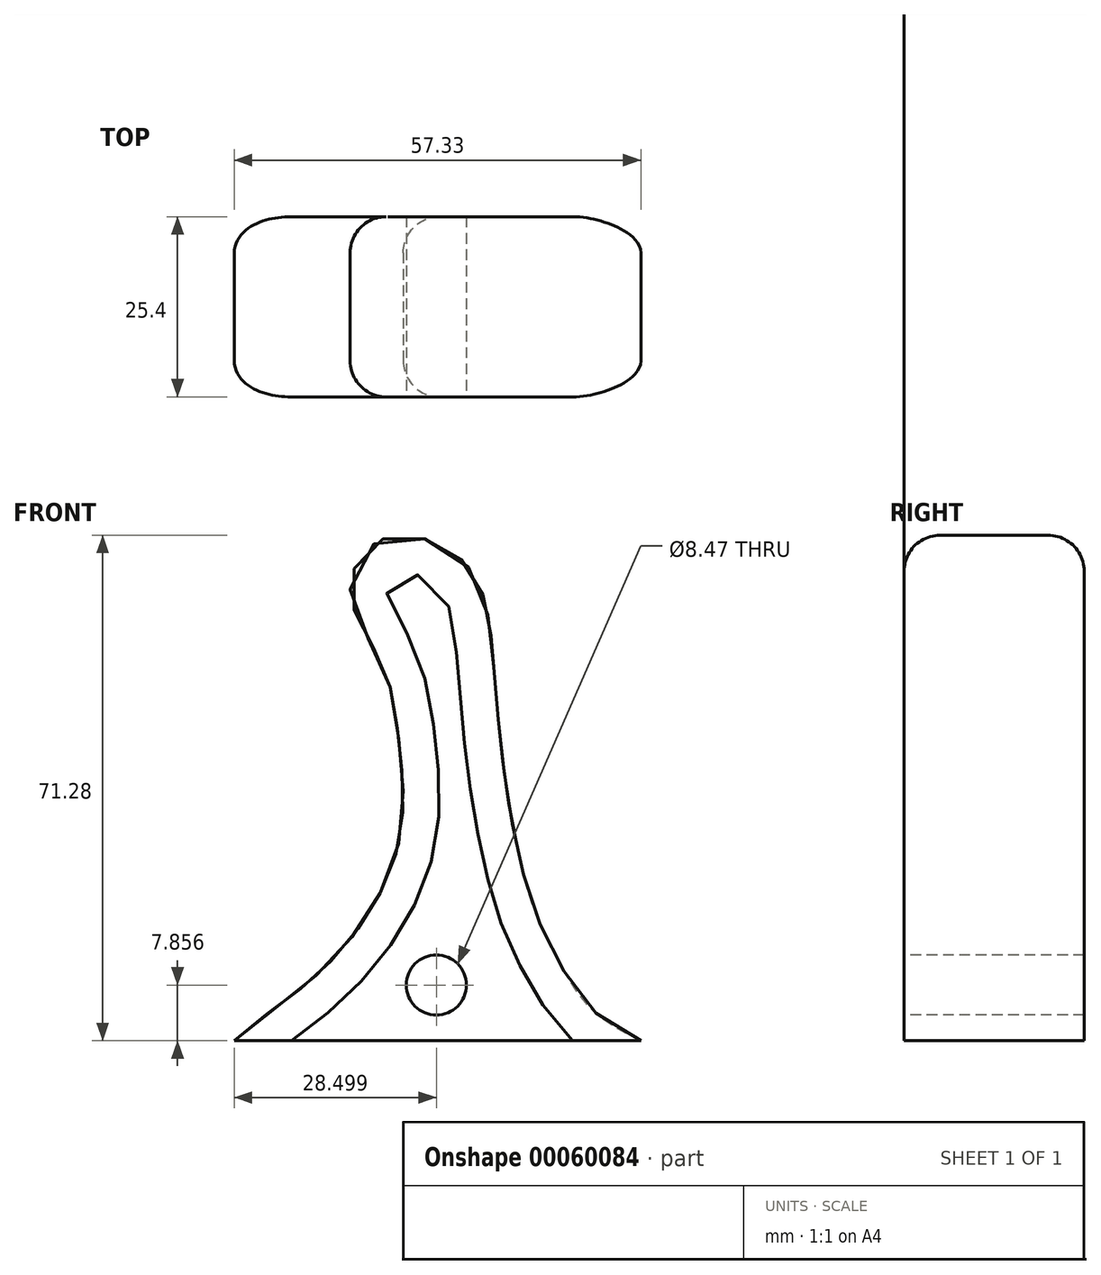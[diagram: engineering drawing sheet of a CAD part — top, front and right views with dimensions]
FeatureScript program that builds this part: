
annotation { "Feature Type Name" : "Feature", "Feature Type Description" : "" }
export const myFeature = defineFeature(function(context is Context, id is Id, definition is map)
    precondition{}
    {
        {
            var Q0;
            Q0=qCreatedBy(makeId("Front.planeOp"),FACE);
            var sketch = newSketch(context, id + "F0", { "sketchPlane" : qUnion([Q0])});
            skFitSpline(sketch, "E0", {"points": [v(-35.6, 0) * mm, v(-27.25, 6.54) * mm, v(-19.41, 14.14) * mm, v(-13.96, 23.16) * mm, v(-11.82, 32.41) * mm, v(-12.53, 43.57) * mm, v(-14.9, 53.3) * mm, v(-19.27, 63.82) * mm, v(-14.4, 70.87) * mm, v(-6.42, 69.77) * mm, v(-2.15, 66.2) * mm, v(0, 60.75) * mm, v(1.27, 49.42) * mm, v(2.84, 35.12) * mm, v(4.78, 25.1) * mm, v(7.04, 17.63) * mm, v(11.13, 9.44) * mm, v(15.79, 3.52) * mm, v(21.72, 0) * mm], "startDerivative": vector(113.36, 115.6) * mm, "endDerivative": vector(129.53, -62.93) * mm});
            skLineSegment(sketch, "E1", {"start": v(-35.6, 0) * mm, "end": v(21.72, 0) * mm});
            skSolve(sketch);
        }
        {
            var Q0;
            Q0=makeQuery(id+"F0.imprint","IMPRINT",FACE,{"disambiguationData":[TD([[makeQuery(id+"F0.imprint","IMPRINT",EDGE,{"derivedFrom":sQuery(id+"F0.wireOp",EDGE,"E0")}),-1.0]])]});
            extrude(context, id + "F1", {"entities" : qUnion([Q0]), "depth" : 25.4 * mm});
        }
        {
            var Q0;
            Q0=makeQuery(id+"F1.opExtrude","CAP_EDGE",EDGE,{"disambiguationData":[OSD([sQuery(id+"F0.wireOp",EDGE,"E0")])],"isStart":false});
            var Q1;
            Q1=makeQuery(id+"F1.opExtrude","CAP_EDGE",EDGE,{"disambiguationData":[OSD([sQuery(id+"F0.wireOp",EDGE,"E0")])],"isStart":true});
            fillet(context, id + "F2", {"entities" : qUnion([Q0, Q1]), "radius" : 5.08 * mm, "tangentPropagation" : true, "allowEdgeOverflow" : false});
        }
        {
            var Q0;
            Q0=makeQuery(id+"F1.opExtrude","CAP_FACE",FACE,{"disambiguationData":[OSD([sQuery(id+"F0.wireOp",EDGE,"E0"),sQuery(id+"F0.wireOp",EDGE,"E1")])],"isStart":false});
            var sketch = newSketch(context, id + "F3", { "sketchPlane" : qUnion([Q0])});
            skCircle(sketch, "E2", {"center": v(-7.11, 7.86) * mm, "radius": 4.24 * mm});
            skSolve(sketch);
        }
        {
            var Q0;
            Q0=makeQuery(id+"F3.imprint","IMPRINT",FACE,{"disambiguationData":[TD([[makeQuery(id+"F3.imprint","IMPRINT",EDGE,{"derivedFrom":sQuery(id+"F3.wireOp",EDGE,"E2")}),1.0]])]});
            extrude(context, id + "F4", {"entities" : qUnion([Q0]), "operationType" : NewBodyOperationType.REMOVE, "oppositeDirection" : true, "depth" : 25.4 * mm});
        }
    });
